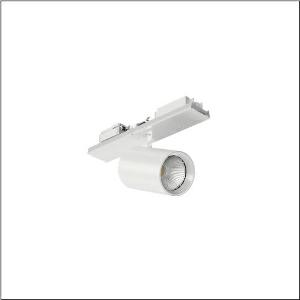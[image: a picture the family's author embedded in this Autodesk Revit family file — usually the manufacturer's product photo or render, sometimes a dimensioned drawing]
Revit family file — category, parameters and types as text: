
# Revit family: licross_r__spot_31_51sl13da43b_6d5a
name_source: partatom
category: Lighting Fixtures
units: mm (PartAtom-declared; Revit-internal decimal feet)

## family parameters
Cut with Voids When Loaded = No
Host = Face
Light Source = No
Part Type = Normal
Room Calculation Point = No
Round Connector Dimension = Use Diameter
Shared = No

## types (1)
- --- (1 x LED, 3680 lm, 28.6 W, 4000K)
    Apparent Load = 29 VA
    CIE Flux Codes = 92 97 99 100 100
    Color Rendering = 90
    Color Temperature = 4000K
    Default Elevation = 1800 mm
    Description = Licross® Spot 31, directional spotlight, light control with lens, of plastic, LED rated luminous flux: 3.680lm, light colour: 940, with plug, 5-pole, mains connection: 220..240V, AC, 50/60Hz, of aluminium, traffic white (RAL 9016), length: 300mm, diameter: 90mm, protection rating (complete): IP20, insulation class (complete): insulation class I (protective earthing), certification: CE, packaging unit: 1 piece
    Height = 175 mm
    Lamp = 1 x LED
    Lamp Light Flux = 3680 lm
    Lamp Power = 28.6 W
    Lamp count = 1
    Length = 90 mm
    Luminous efficacy = 129 lm/W
    Manufacturer = Siteco
    ModVariant = No
    Model = 51SL13DA43B
    Mounting Place = Ceiling
    Mounting Type = Pendant
    Number of Poles = 1
    OnlyDefault = Yes
    Power Factor = 1
    Product Name = Licross® Spot 31
    Product group = directional spotlight
    ProductGroupID = 905
    Protection Class = Protection class I
    Protection Degree = IP 20
    RLX_Detail_Level = 1
    RLX_Emergency_Light_Flux = 0 lm
    RLX_Emergency_Type = 0
    RLX_Emergency_Type_DB = No
    RlxData = <blob elided: 14801 chars, md5=20ec88e5>
    Socket = socket
    Standby Power = 0 W
    System Light Flux = 3680 lm
    System Power = 29 W
    Type Comments = factory setting: luminous flux: 100 % | (ON | ON | ON) | 700 mA
    Type Image = l_1245720.jpg
    URL = http://relux.com
    VarID = @adj_102339
    Voltage = 0 V
    Weight = 0.00 kg
    Width = 0 mm  [stored 0 ft]

note: [stored X ft] marks values corroborated as IEEE doubles in the binary element streams (Revit-internal decimal feet)

## geometry (parser evidence)
native form markers: Sweep x13
no freeform markers — native parametric forms only
